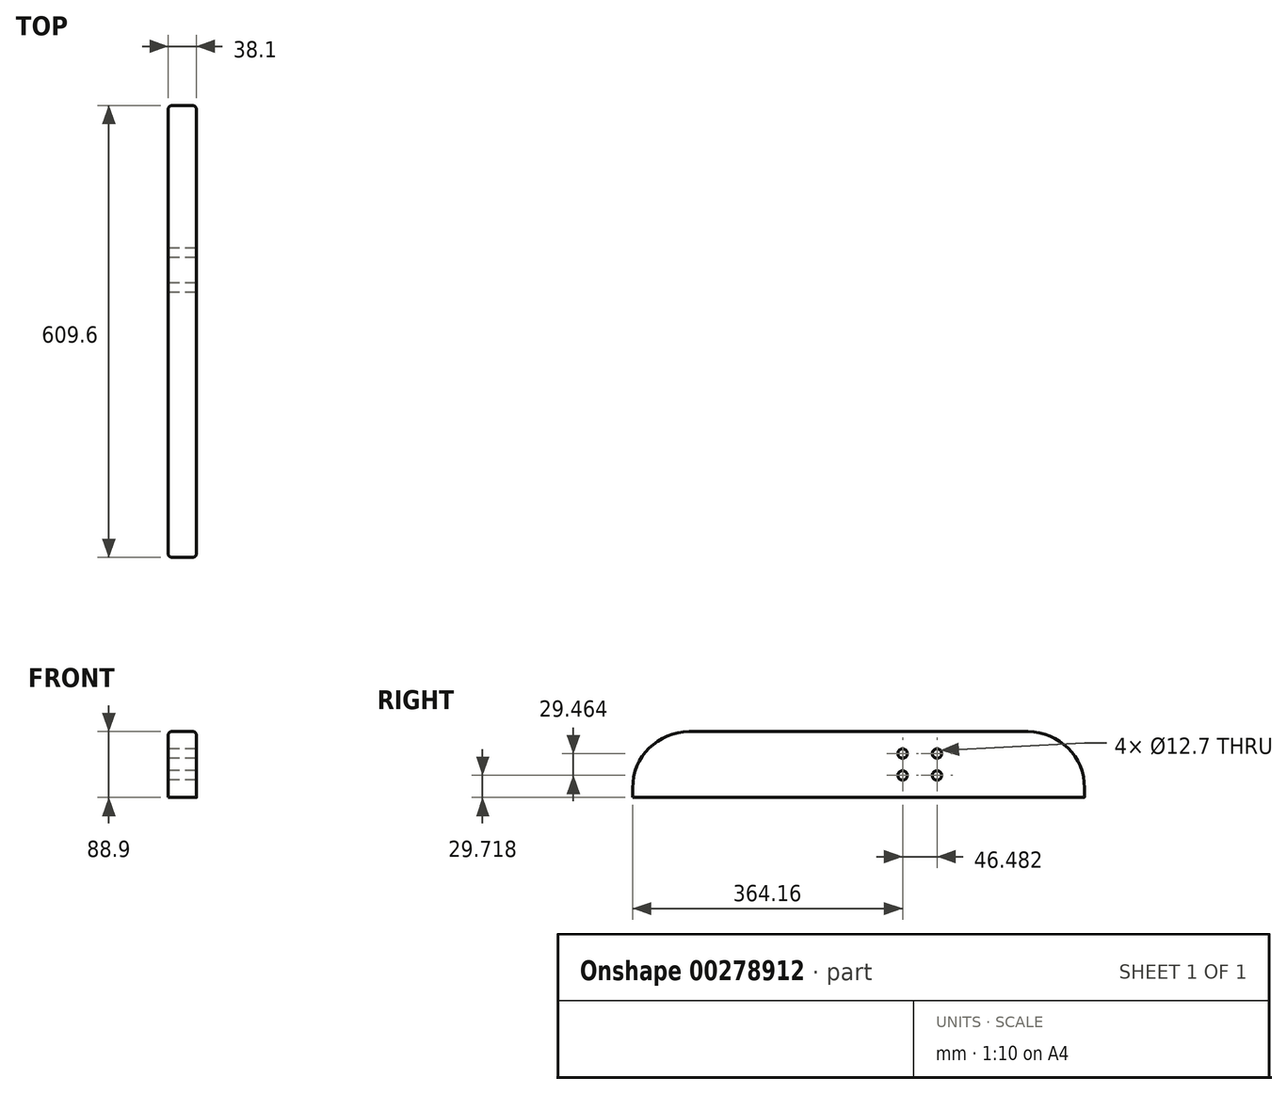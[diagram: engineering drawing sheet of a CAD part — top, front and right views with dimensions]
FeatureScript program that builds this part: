
annotation { "Feature Type Name" : "Feature", "Feature Type Description" : "" }
export const myFeature = defineFeature(function(context is Context, id is Id, definition is map)
    precondition{}
    {
        {
            var Q0;
            Q0=qCreatedBy(makeId("Front.planeOp"),FACE);
            var sketch = newSketch(context, id + "F0", { "sketchPlane" : qUnion([Q0])});
            skLineSegment(sketch, "E0.bottom", {"start": v(19.05, 44.45) * mm, "end": v(-19.05, 44.45) * mm});
            skLineSegment(sketch, "E0.top", {"start": v(19.05, -44.45) * mm, "end": v(-19.05, -44.45) * mm});
            skLineSegment(sketch, "E0.left", {"start": v(19.05, 44.45) * mm, "end": v(19.05, -44.45) * mm});
            skLineSegment(sketch, "E0.right", {"start": v(-19.05, 44.45) * mm, "end": v(-19.05, -44.45) * mm});
            skPoint(sketch, "E0.middle", {"position": v(0, 0) * mm});
            skSolve(sketch);
        }
        {
            var Q0;
            Q0=qSketchRegion(id+"F0",true);
            extrude(context, id + "F1", {"entities" : qUnion([Q0]), "oppositeDirection" : true, "depth" : 609.6 * mm});
        }
        {
            var Q0;
            Q0=makeQuery(id+"F1.opExtrude","SWEPT_FACE",FACE,{"disambiguationData":[OSD([sQuery(id+"F0.wireOp",EDGE,"E0.right")])]});
            var sketch = newSketch(context, id + "F2", { "sketchPlane" : qUnion([Q0])});
            skCircle(sketch, "E1", {"center": v(-410.64, 14.73) * mm, "radius": 6.35 * mm});
            skCircle(sketch, "E2.0.1.0", {"center": v(-410.64, -14.73) * mm, "radius": 6.35 * mm});
            skCircle(sketch, "E2.1.0.0", {"center": v(-364.16, 14.73) * mm, "radius": 6.35 * mm});
            skCircle(sketch, "E2.1.1.0", {"center": v(-364.16, -14.73) * mm, "radius": 6.35 * mm});
            skLineSegment(sketch, "E2.direction1", {"start": v(-410.64, 14.73) * mm, "end": v(-364.16, 14.73) * mm, "construction": true});
            skLineSegment(sketch, "E2.direction2", {"start": v(-410.64, 14.73) * mm, "end": v(-410.64, -14.73) * mm, "construction": true});
            skSolve(sketch);
        }
        {
            var Q0;
            Q0=qSketchRegion(id+"F2",true);
            extrude(context, id + "F3", {"entities" : qUnion([Q0]), "operationType" : NewBodyOperationType.REMOVE, "oppositeDirection" : true, "depth" : 38.1 * mm});
        }
        {
            var Q0;
            Q0=makeQuery(id+"F1.opExtrude","CAP_EDGE",EDGE,{"disambiguationData":[OSD([sQuery(id+"F0.wireOp",EDGE,"E0.bottom")])],"isStart":false});
            var Q1;
            Q1=makeQuery(id+"F1.opExtrude","CAP_EDGE",EDGE,{"disambiguationData":[OSD([sQuery(id+"F0.wireOp",EDGE,"E0.bottom")])],"isStart":true});
            fillet(context, id + "F4", {"entities" : qUnion([Q0, Q1]), "radius" : 76.2 * mm, "tangentPropagation" : true, "allowEdgeOverflow" : false});
        }
        {
            var Q0;
            Q0=makeQuery(id+"F1.opExtrude","SWEPT_EDGE",EDGE,{"disambiguationData":[OSD([sQuery(id+"F0.wireOp",EDGE,"E0.bottom"),sQuery(id+"F0.wireOp",EDGE,"E0.right")])]});
            var Q1;
            Q1=makeQuery(id+"F1.opExtrude","SWEPT_EDGE",EDGE,{"disambiguationData":[OSD([sQuery(id+"F0.wireOp",EDGE,"E0.bottom"),sQuery(id+"F0.wireOp",EDGE,"E0.left")])]});
            fillet(context, id + "F5", {"entities" : qUnion([Q0, Q1]), "radius" : 5.08 * mm, "tangentPropagation" : true, "allowEdgeOverflow" : false});
        }
    });
